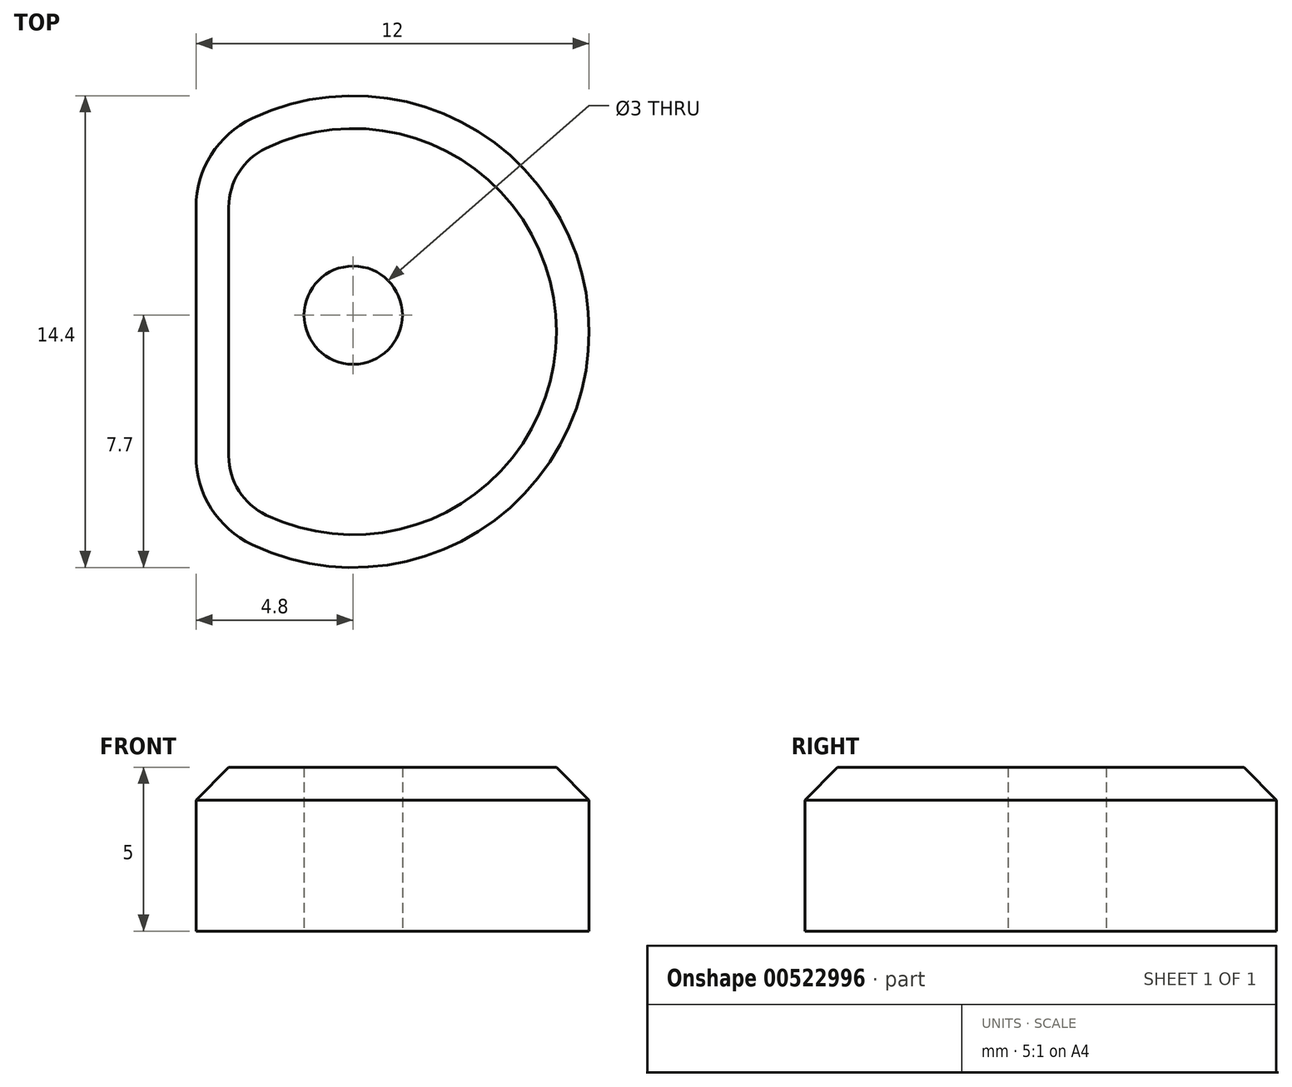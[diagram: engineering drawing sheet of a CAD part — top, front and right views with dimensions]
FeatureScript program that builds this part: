
annotation { "Feature Type Name" : "Feature", "Feature Type Description" : "" }
export const myFeature = defineFeature(function(context is Context, id is Id, definition is map)
    precondition{}
    {
        {
            var Q0;
            Q0=qCreatedBy(makeId("Top.planeOp"),FACE);
            var sketch = newSketch(context, id + "F0", { "sketchPlane" : qUnion([Q0])});
            skCircle(sketch, "E0", {"center": v(0, 0) * mm, "radius": 1.5 * mm});
            skLineSegment(sketch, "E1", {"start": v(0, 0) * mm, "end": v(0, -0.5) * mm, "construction": true});
            skArc(sketch, "E2", {"start": v(-3.09, -7) * mm, "mid": v(7.2, -0.5) * mm, "end": v(-3.09, 6) * mm});
            skLineSegment(sketch, "E3", {"start": v(-4.8, 3.3) * mm, "end": v(-4.8, -4.3) * mm});
            skPoint(sketch, "E4.visualSharp", {"position": v(-4.8, 4.87) * mm});
            skArc(sketch, "E4.filletArc", {"start": v(-3.09, 6) * mm, "mid": v(-4.34, 4.9) * mm, "end": v(-4.8, 3.3) * mm});
            skPoint(sketch, "E5.visualSharp", {"position": v(-4.8, -5.87) * mm});
            skArc(sketch, "E5.filletArc", {"start": v(-4.8, -4.3) * mm, "mid": v(-4.34, -5.9) * mm, "end": v(-3.09, -7) * mm});
            skSolve(sketch);
        }
        {
            var Q0;
            Q0=qSketchRegion(id+"F0",true);
            extrude(context, id + "F1", {"entities" : qUnion([Q0]), "depth" : 5 * mm});
        }
        {
            var Q0;
            Q0=makeQuery(id+"F1.opExtrude","CAP_EDGE",EDGE,{"disambiguationData":[OSD([sQuery(id+"F0.wireOp",EDGE,"E2")])],"isStart":false});
            chamfer(context, id + "F2", {"entities" : qUnion([Q0]), "width" : 1 * mm, "tangentPropagation" : true});
        }
    });
